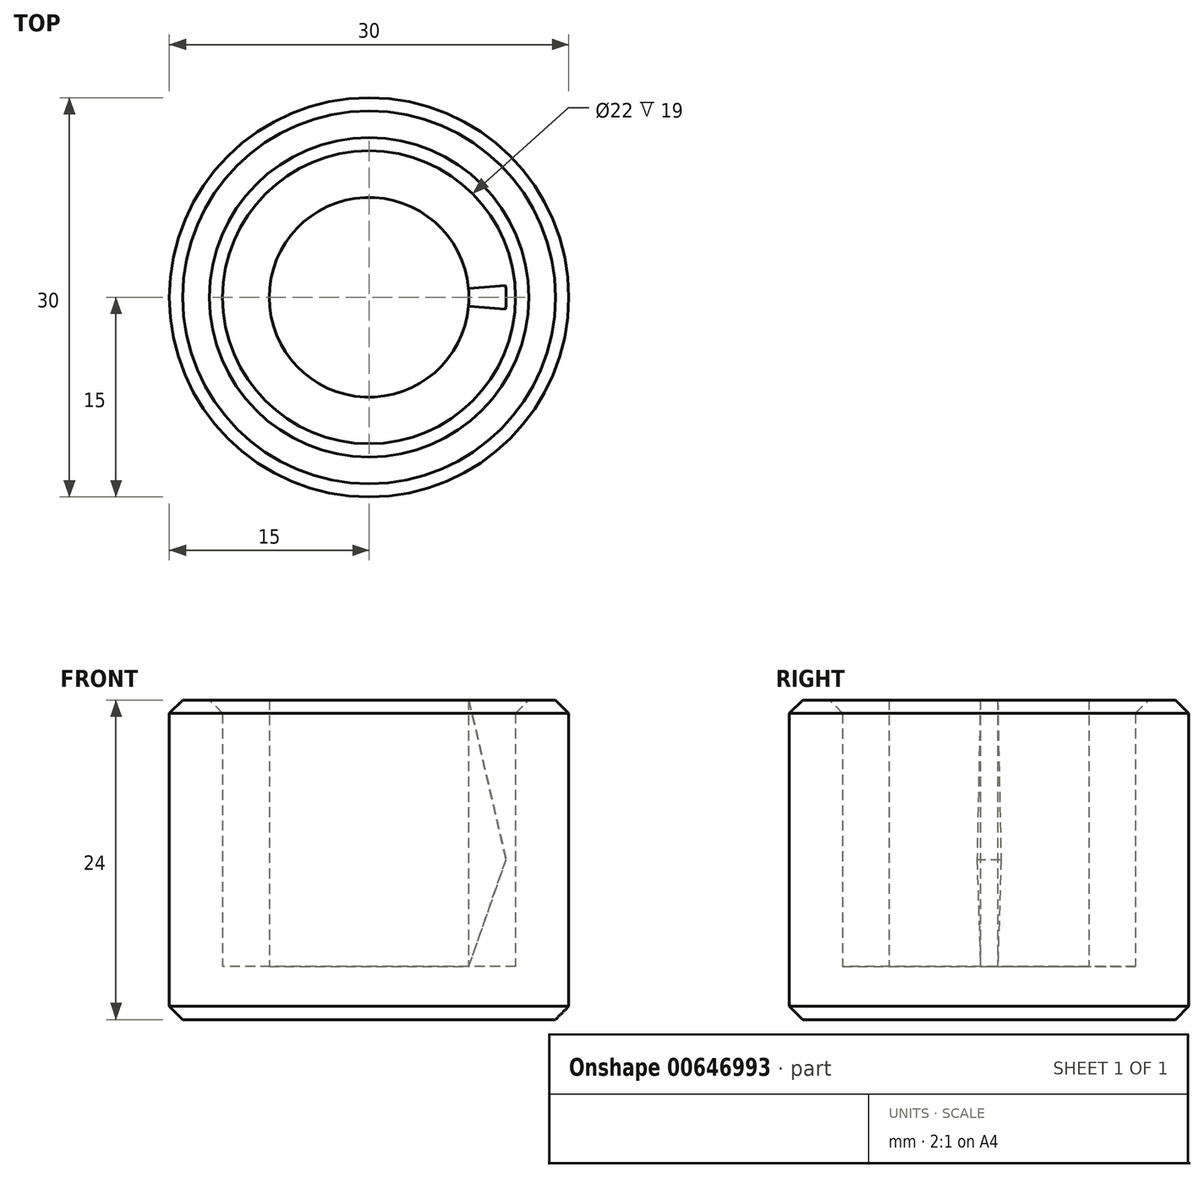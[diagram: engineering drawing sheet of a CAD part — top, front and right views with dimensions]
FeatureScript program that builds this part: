
annotation { "Feature Type Name" : "Feature", "Feature Type Description" : "" }
export const myFeature = defineFeature(function(context is Context, id is Id, definition is map)
    precondition{}
    {
        {
            var Q0;
            Q0=qCreatedBy(makeId("Top.planeOp"),FACE);
            var sketch = newSketch(context, id + "F0", { "sketchPlane" : qUnion([Q0])});
            skCircle(sketch, "E0", {"center": v(0, 0) * mm, "radius": 11 * mm});
            skCircle(sketch, "E1", {"center": v(0, 0) * mm, "radius": 15 * mm});
            skCircle(sketch, "E2", {"center": v(0, 0) * mm, "radius": 7.5 * mm});
            skSolve(sketch);
        }
        {
            var Q0;
            Q0 = qSketchRegion(id + "F0", true);
            var Q1;
            Q1=makeQuery(id+"F0.imprint","IMPRINT",FACE,{"disambiguationData":[TD([[makeQuery(id+"F0.imprint","IMPRINT",EDGE,{"derivedFrom":sQuery(id+"F0.wireOp",EDGE,"E2")}),1.0]])]});
            var Q2;
            Q2=makeQuery(id+"F0.imprint","IMPRINT",FACE,{"disambiguationData":[TD([[makeQuery(id+"F0.imprint","IMPRINT",EDGE,{"derivedFrom":sQuery(id+"F0.wireOp",EDGE,"E0")}),1.0]])]});
            extrude(context, id + "F1", {"entities" : qUnion([Q0, Q1, Q2]), "oppositeDirection" : true, "depth" : 4 * mm, "offsetDistance" : 25 * mm});
        }
        {
            var Q0;
            Q0=makeQuery(id+"F0.imprint","IMPRINT",FACE,{"disambiguationData":[TD([[makeQuery(id+"F0.imprint","IMPRINT",EDGE,{"derivedFrom":sQuery(id+"F0.wireOp",EDGE,"E2")}),1.0]])]});
            var Q1;
            Q1=makeQuery(id+"F0.imprint","IMPRINT",FACE,{"disambiguationData":[TD([[makeQuery(id+"F0.imprint","IMPRINT",EDGE,{"derivedFrom":sQuery(id+"F0.wireOp",EDGE,"E0")}),-1.0]])]});
            extrude(context, id + "F2", {"entities" : qUnion([Q0, Q1]), "operationType" : NewBodyOperationType.ADD, "depth" : 20 * mm, "offsetDistance" : 25 * mm});
        }
        {
            var Q0;
            Q0=qCreatedBy(makeId("Front.planeOp"),FACE);
            var sketch = newSketch(context, id + "F3", { "sketchPlane" : qUnion([Q0])});
            skLineSegment(sketch, "E3", {"start": v(0, 0) * mm, "end": v(0, 20) * mm});
            skLineSegment(sketch, "E4", {"start": v(0, 20) * mm, "end": v(7.5, 20) * mm});
            skLineSegment(sketch, "E5", {"start": v(7.5, 20) * mm, "end": v(10.3, 8) * mm});
            skLineSegment(sketch, "E6", {"start": v(10.3, 8) * mm, "end": v(7.5, 0) * mm});
            skLineSegment(sketch, "E7", {"start": v(7.5, 0) * mm, "end": v(0, 0) * mm});
            skSolve(sketch);
        }
        {
            var Q0;
            Q0 = qSketchRegion(id + "F3", true);
            var Q1;
            Q1=sQuery(id+"F3.wireOp",EDGE,"E3");
            revolve(context, id + "F4", {"operationType" : NewBodyOperationType.ADD, "entities" : qUnion([Q0]), "axis" : qUnion([Q1]), "revolveType" : RevolveType.SYMMETRIC, "angle" : 10 * degree});
        }
        {
            var Q0;
            Q0=makeQuery(id+"F2.opExtrude","CAP_FACE",FACE,{"disambiguationData":[OSD([sQuery(id+"F0.wireOp",EDGE,"E0"),sQuery(id+"F0.wireOp",EDGE,"E1")])],"isStart":false});
            var Q1;
            Q1=makeQuery(id+"F1.opExtrude","CAP_FACE",FACE,{"disambiguationData":[OSD([sQuery(id+"F0.wireOp",EDGE,"E1")])],"isStart":false});
            chamfer(context, id + "F5", {"entities" : qUnion([Q0, Q1]), "width" : 1 * mm, "tangentPropagation" : true});
        }
    });
